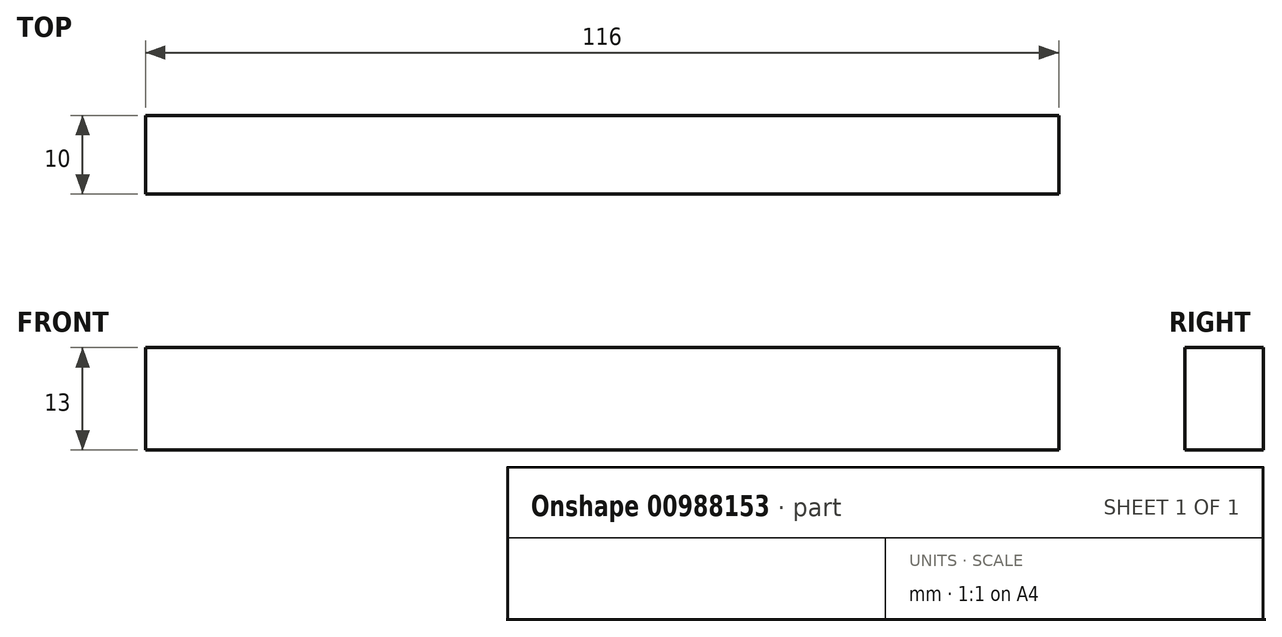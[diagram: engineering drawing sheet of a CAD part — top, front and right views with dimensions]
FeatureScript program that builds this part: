
annotation { "Feature Type Name" : "Feature", "Feature Type Description" : "" }
export const myFeature = defineFeature(function(context is Context, id is Id, definition is map)
    precondition{}
    {
        {
            var Q0;
            Q0=qCreatedBy(makeId("Front.planeOp"),FACE);
            var sketch = newSketch(context, id + "F0", { "sketchPlane" : qUnion([Q0])});
            skLineSegment(sketch, "E0", {"start": v(0, 0) * mm, "end": v(116, 0) * mm});
            skLineSegment(sketch, "E1", {"start": v(116, 0) * mm, "end": v(116, 13) * mm});
            skLineSegment(sketch, "E2", {"start": v(116, 13) * mm, "end": v(0, 13) * mm});
            skLineSegment(sketch, "E3", {"start": v(0, 13) * mm, "end": v(0, 0) * mm});
            skSolve(sketch);
        }
        {
            var Q0;
            Q0=makeQuery(id+"F0.imprint","IMPRINT",FACE,{"disambiguationData":[TD([[makeQuery(id+"F0.imprint","IMPRINT",EDGE,{"derivedFrom":sQuery(id+"F0.wireOp",EDGE,"E0")}),1.0]])]});
            extrude(context, id + "F1", {"entities" : qUnion([Q0]), "depth" : 10 * mm, "offsetDistance" : 25 * mm});
        }
    });
